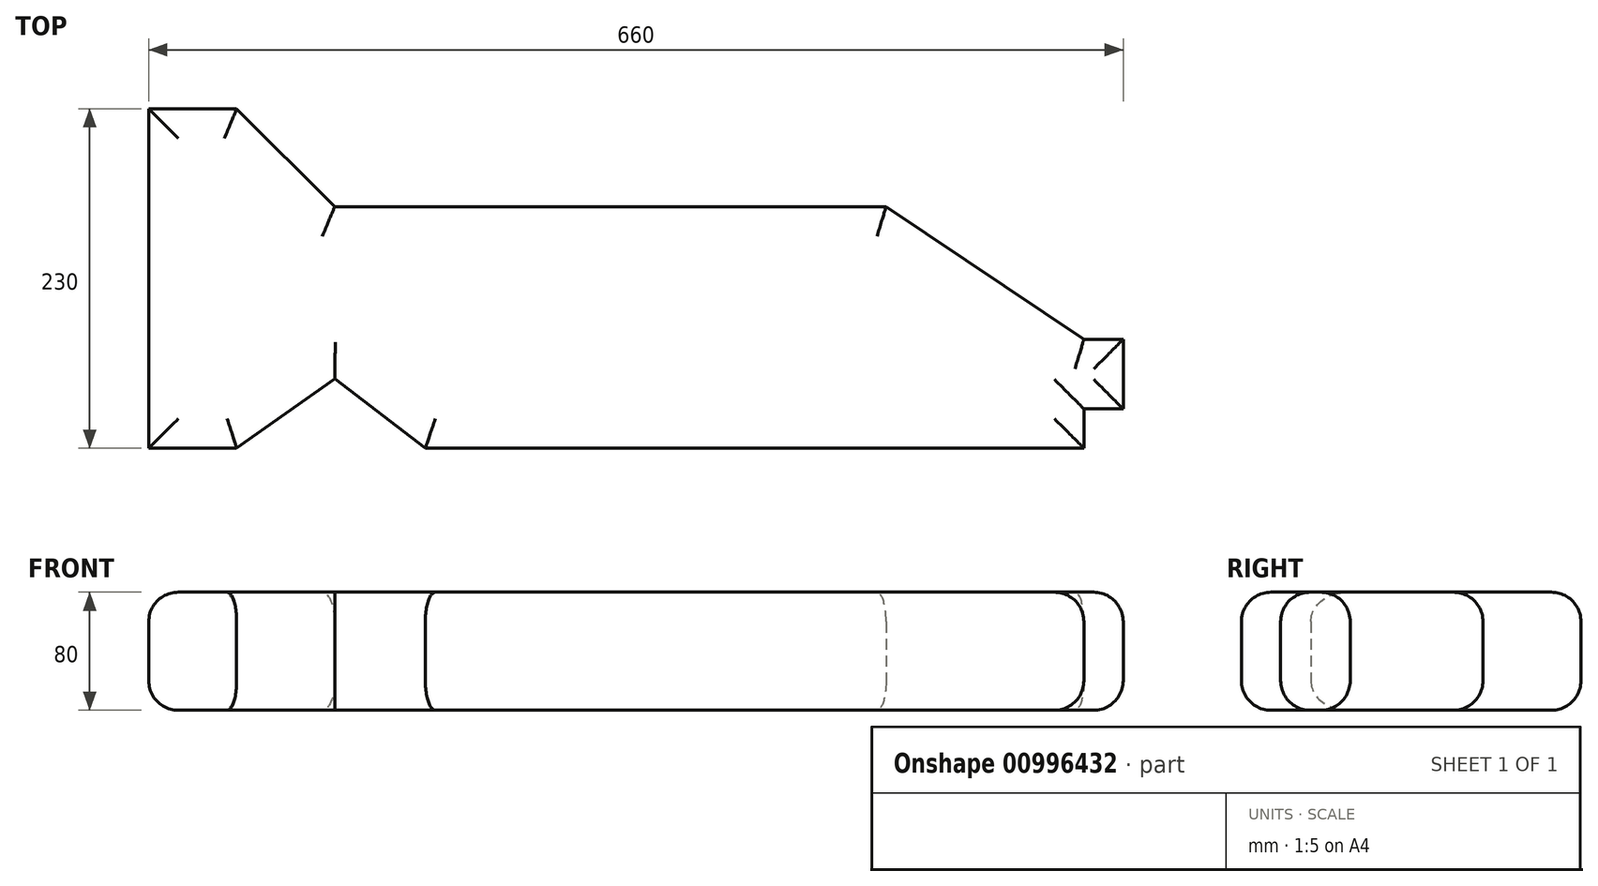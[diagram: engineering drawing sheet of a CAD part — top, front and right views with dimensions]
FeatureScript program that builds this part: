
annotation { "Feature Type Name" : "Feature", "Feature Type Description" : "" }
export const myFeature = defineFeature(function(context is Context, id is Id, definition is map)
    precondition{}
    {
        {
            var Q0;
            Q0=qCreatedBy(makeId("Top.planeOp"),FACE);
            var sketch = newSketch(context, id + "F0", { "sketchPlane" : qUnion([Q0])});
            skLineSegment(sketch, "E0.bottom", {"start": v(-270.44, 115) * mm, "end": v(-330, 115) * mm});
            skLineSegment(sketch, "E0.top", {"start": v(303.37, -115) * mm, "end": v(-142.65, -115) * mm});
            skLineSegment(sketch, "E0.left", {"start": v(330, -41.27) * mm, "end": v(330, -88.41) * mm});
            skLineSegment(sketch, "E0.right", {"start": v(-330, 115) * mm, "end": v(-330, -115) * mm});
            skPoint(sketch, "E0.middle", {"position": v(0, 0) * mm});
            skLineSegment(sketch, "E1", {"start": v(-330, 115) * mm, "end": v(-270.44, 115) * mm});
            skLineSegment(sketch, "E2", {"start": v(-270.44, 115) * mm, "end": v(-204.06, 48.68) * mm});
            skLineSegment(sketch, "E3", {"start": v(-204.06, 48.68) * mm, "end": v(169.38, 48.68) * mm});
            skLineSegment(sketch, "E4", {"start": v(169.38, 48.68) * mm, "end": v(303.37, -41.27) * mm});
            skLineSegment(sketch, "E5", {"start": v(303.37, -41.27) * mm, "end": v(330, -41.27) * mm});
            skLineSegment(sketch, "E6", {"start": v(-270.44, -115) * mm, "end": v(-204.06, -67.94) * mm});
            skLineSegment(sketch, "E7", {"start": v(-204.06, -67.94) * mm, "end": v(-142.65, -115) * mm});
            skLineSegment(sketch, "E8", {"start": v(303.37, -115) * mm, "end": v(303.37, -88.41) * mm});
            skLineSegment(sketch, "E9", {"start": v(303.37, -88.41) * mm, "end": v(330, -88.41) * mm});
            skLineSegment(sketch, "E10.trimOffspring", {"start": v(-270.44, -115) * mm, "end": v(-330, -115) * mm});
            skPoint(sketch, "E11.orphan", {"position": v(330, -115) * mm});
            skPoint(sketch, "E12.orphan", {"position": v(330, 115) * mm});
            skSolve(sketch);
        }
        {
            var Q0;
            Q0 = qSketchRegion(id + "F0", true);
            extrude(context, id + "F1", {"entities" : qUnion([Q0]), "endBound" : BoundingType.SYMMETRIC, "depth" : 80 * mm, "offsetDistance" : 25 * mm});
        }
        {
            var Q0;
            Q0=makeQuery(id+"F1.opExtrude","CAP_FACE",FACE,{"disambiguationData":[OSD([sQuery(id+"F0.wireOp",EDGE,"E0.top"),sQuery(id+"F0.wireOp",EDGE,"E0.left"),sQuery(id+"F0.wireOp",EDGE,"E0.right"),sQuery(id+"F0.wireOp",EDGE,"E1"),sQuery(id+"F0.wireOp",EDGE,"E2"),sQuery(id+"F0.wireOp",EDGE,"E3"),sQuery(id+"F0.wireOp",EDGE,"E4"),sQuery(id+"F0.wireOp",EDGE,"E5"),sQuery(id+"F0.wireOp",EDGE,"E6"),sQuery(id+"F0.wireOp",EDGE,"E7"),sQuery(id+"F0.wireOp",EDGE,"E8"),sQuery(id+"F0.wireOp",EDGE,"E9"),sQuery(id+"F0.wireOp",EDGE,"E10.trimOffspring")])],"isStart":false});
            var Q1;
            Q1=makeQuery(id+"F1.opExtrude","CAP_FACE",FACE,{"disambiguationData":[OSD([sQuery(id+"F0.wireOp",EDGE,"E0.top"),sQuery(id+"F0.wireOp",EDGE,"E0.left"),sQuery(id+"F0.wireOp",EDGE,"E0.right"),sQuery(id+"F0.wireOp",EDGE,"E1"),sQuery(id+"F0.wireOp",EDGE,"E2"),sQuery(id+"F0.wireOp",EDGE,"E3"),sQuery(id+"F0.wireOp",EDGE,"E4"),sQuery(id+"F0.wireOp",EDGE,"E5"),sQuery(id+"F0.wireOp",EDGE,"E6"),sQuery(id+"F0.wireOp",EDGE,"E7"),sQuery(id+"F0.wireOp",EDGE,"E8"),sQuery(id+"F0.wireOp",EDGE,"E9"),sQuery(id+"F0.wireOp",EDGE,"E10.trimOffspring")])],"isStart":true});
            fillet(context, id + "F2", {"entities" : qUnion([Q0, Q1]), "radius" : 20 * mm, "tangentPropagation" : true, "allowEdgeOverflow" : false});
        }
    });
